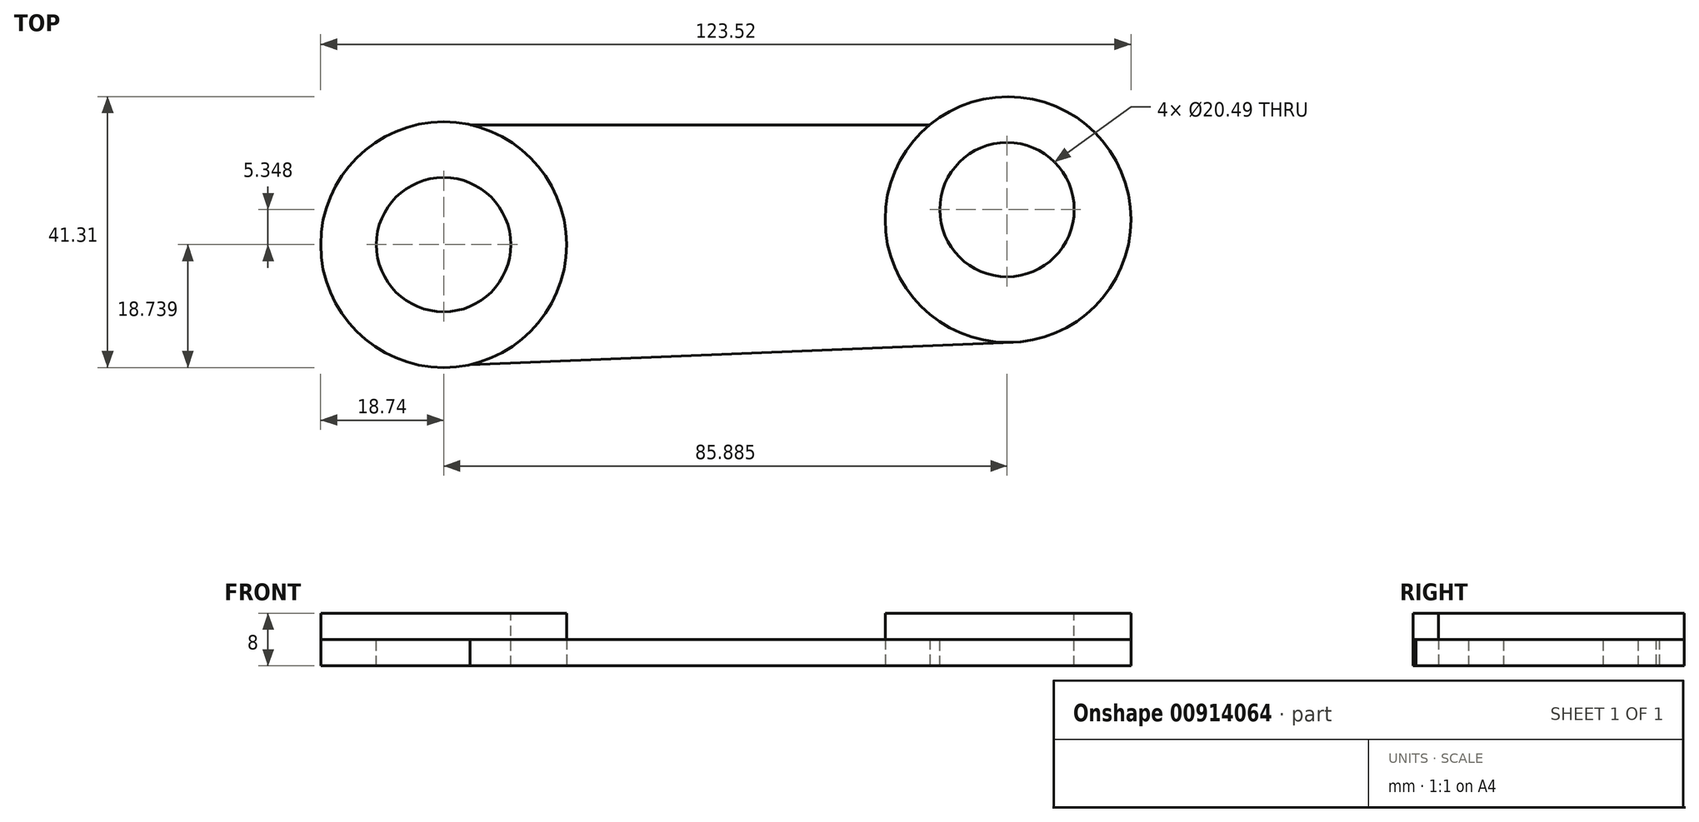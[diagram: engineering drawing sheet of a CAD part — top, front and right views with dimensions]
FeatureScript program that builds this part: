
annotation { "Feature Type Name" : "Feature", "Feature Type Description" : "" }
export const myFeature = defineFeature(function(context is Context, id is Id, definition is map)
    precondition{}
    {
        {
            var Q0;
            Q0=qCreatedBy(makeId("Top.planeOp"),FACE);
            var sketch = newSketch(context, id + "F0", { "sketchPlane" : qUnion([Q0])});
            skCircle(sketch, "E0", {"center": v(-52.93, 39.08) * mm, "radius": 18.74 * mm});
            skCircle(sketch, "E1", {"center": v(33.11, 42.91) * mm, "radius": 18.74 * mm});
            skLineSegment(sketch, "E2", {"start": v(-48.81, 57.36) * mm, "end": v(21.18, 57.36) * mm});
            skLineSegment(sketch, "E3", {"start": v(-48.9, 20.78) * mm, "end": v(33.88, 24.19) * mm});
            skSolve(sketch);
        }
        {
            var Q0;
            {var subQ0=sQuery(id+"F0.wireOp",EDGE,"E0");var subQ1=makeQuery(id+"F0.imprint","INTERSECT",VERTEX,{"derivedFrom":[subQ0,sQuery(id+"F0.wireOp",EDGE,"E2")]});Q0=makeQuery(id+"F0.imprint","IMPRINT",FACE,{"disambiguationData":[TD([[makeQuery(id+"F0.imprint","IMPRINT",EDGE,{"disambiguationData":[TD([[subQ1,-1.0]])],"derivedFrom":subQ0}),1.0]])]});}
            var Q1;
            {var subQ0=sQuery(id+"F0.wireOp",EDGE,"E1");var subQ1=makeQuery(id+"F0.imprint","INTERSECT",VERTEX,{"derivedFrom":[subQ0,sQuery(id+"F0.wireOp",EDGE,"E2")]});Q1=makeQuery(id+"F0.imprint","IMPRINT",FACE,{"disambiguationData":[TD([[makeQuery(id+"F0.imprint","IMPRINT",EDGE,{"disambiguationData":[TD([[subQ1,-1.0]])],"derivedFrom":subQ0}),1.0]])]});}
            extrude(context, id + "F1", {"entities" : qUnion([Q0, Q1]), "depth" : 8 * mm, "offsetDistance" : 25 * mm});
        }
        {
            var Q0;
            Q0 = qSketchRegion(id + "F0", true);
            extrude(context, id + "F2", {"entities" : qUnion([Q0]), "depth" : 4 * mm, "offsetDistance" : 25 * mm});
        }
        {
            var Q0;
            Q0=makeQuery(id+"F1.opExtrude","CAP_FACE",FACE,{"disambiguationData":[OSD([sQuery(id+"F0.wireOp",EDGE,"E0")])],"isStart":false});
            var sketch = newSketch(context, id + "F3", { "sketchPlane" : qUnion([Q0])});
            skCircle(sketch, "E4", {"center": v(-52.93, 39.08) * mm, "radius": 10.25 * mm});
            skCircle(sketch, "E5", {"center": v(32.96, 44.43) * mm, "radius": 10.25 * mm});
            skSolve(sketch);
        }
        {
            var Q0;
            Q0=sQuery(id+"F3.wireOp",VERTEX,"E4.center");
            var Q1;
            Q1=sQuery(id+"F3.wireOp",VERTEX,"E5.center");
            var Q2;
            Q2=makeQuery(id+"F1.opExtrude","SWEPT_BODY",BODY,{"disambiguationData":[OSD([sQuery(id+"F0.wireOp",EDGE,"E0")])]});
            var Q3;
            Q3=makeQuery(id+"F1.opExtrude","SWEPT_BODY",BODY,{"disambiguationData":[OSD([sQuery(id+"F0.wireOp",EDGE,"E1")])]});
            var Q4;
            Q4=makeQuery(id+"F2.opExtrude","SWEPT_BODY",BODY,{"disambiguationData":[OSD([sQuery(id+"F0.wireOp",EDGE,"E0"),sQuery(id+"F0.wireOp",EDGE,"E1"),sQuery(id+"F0.wireOp",EDGE,"E2"),sQuery(id+"F0.wireOp",EDGE,"E3")])]});
            hole(context, id + "F4", {"style" : HoleStyle.SIMPLE, "endStyle" : HoleEndStyle.BLIND, "holeDiameter" : 20.49 * mm, "majorDiameter" : 5 * mm, "holeDepth" : 12 * mm, "isTappedThrough" : true, "tappedDepth" : 12 * mm, "tapClearance" : 3, "locations" : qUnion([Q0, Q1]), "scope" : qUnion([Q2, Q3, Q4])});
        }
    });
